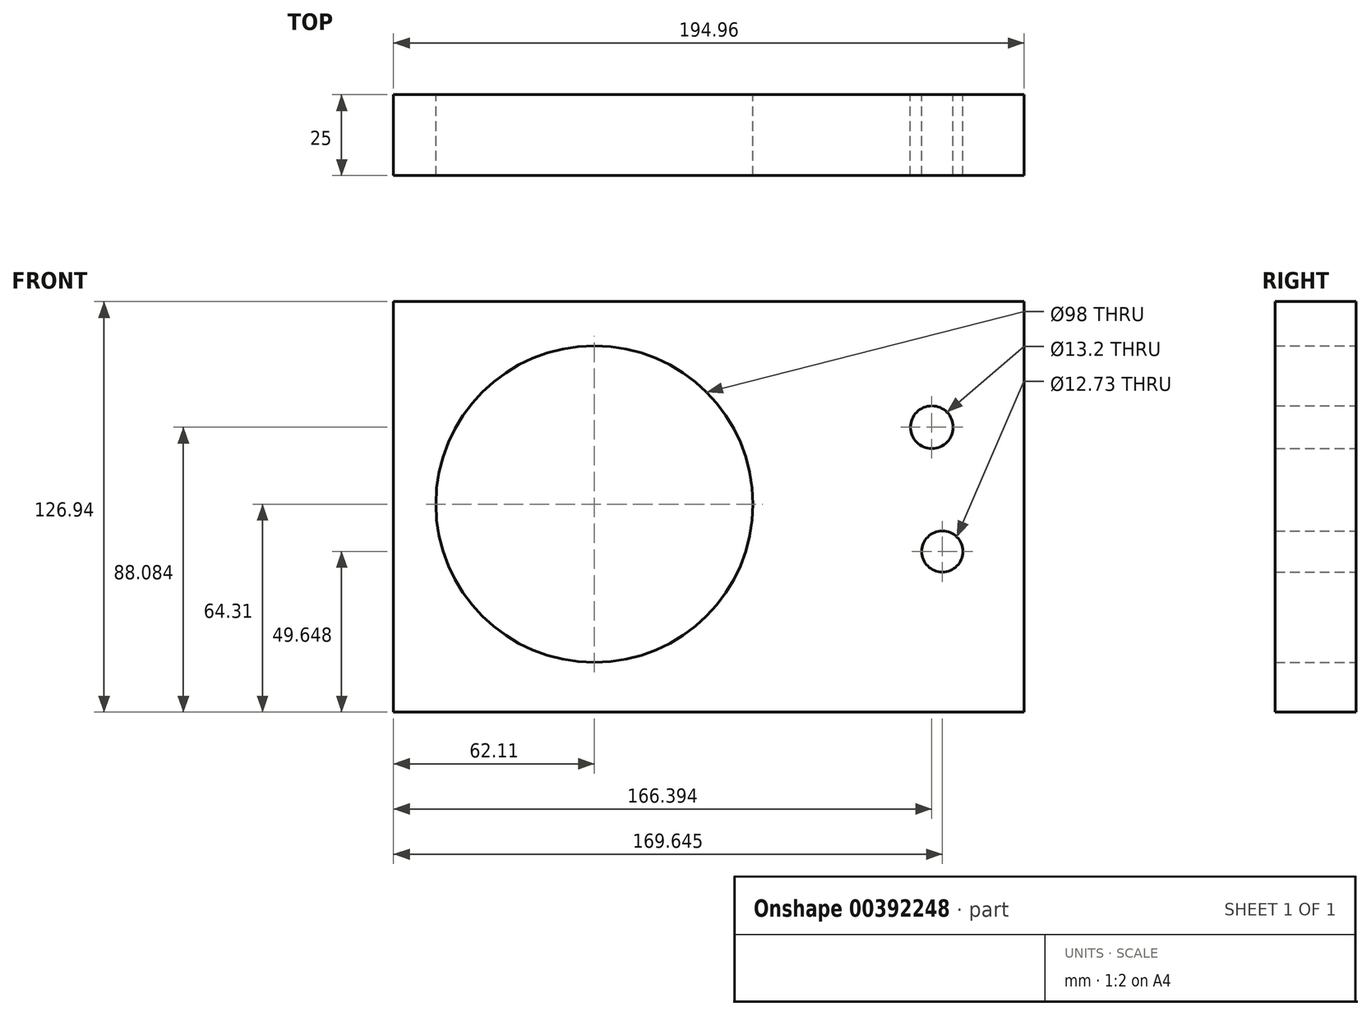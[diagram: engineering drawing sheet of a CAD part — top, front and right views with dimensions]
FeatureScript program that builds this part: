
annotation { "Feature Type Name" : "Feature", "Feature Type Description" : "" }
export const myFeature = defineFeature(function(context is Context, id is Id, definition is map)
    precondition{}
    {
        {
            var Q0;
            Q0=qCreatedBy(makeId("Front.planeOp"),FACE);
            var sketch = newSketch(context, id + "F0", { "sketchPlane" : qUnion([Q0])});
            skCircle(sketch, "E0", {"center": v(0, 0) * mm, "radius": 49 * mm});
            skLineSegment(sketch, "E1.bottom", {"start": v(-62.1, 62.63) * mm, "end": v(132.85, 62.63) * mm});
            skLineSegment(sketch, "E1.top", {"start": v(-62.1, -64.31) * mm, "end": v(132.85, -64.31) * mm});
            skLineSegment(sketch, "E1.left", {"start": v(-62.1, 62.63) * mm, "end": v(-62.1, -64.31) * mm});
            skLineSegment(sketch, "E1.right", {"start": v(132.85, 62.63) * mm, "end": v(132.85, -64.31) * mm});
            skCircle(sketch, "E2", {"center": v(104.28, 23.77) * mm, "radius": 6.6 * mm});
            skCircle(sketch, "E3", {"center": v(107.54, -14.66) * mm, "radius": 6.37 * mm});
            skSolve(sketch);
        }
        {
            var Q0;
            Q0 = qSketchRegion(id + "F0", true);
            extrude(context, id + "F1", {"entities" : qUnion([Q0]), "depth" : 25 * mm});
        }
        {
            var Q0;
            Q0=makeQuery(id+"F1.opExtrude","SWEPT_FACE",FACE,{"disambiguationData":[OSD([sQuery(id+"F0.wireOp",EDGE,"E1.bottom")])]});
            var sketch = newSketch(context, id + "F2", { "sketchPlane" : qUnion([Q0])});
            skPoint(sketch, "E4.0", {"position": v(0, 0) * mm});
            skSolve(sketch);
        }
    });
